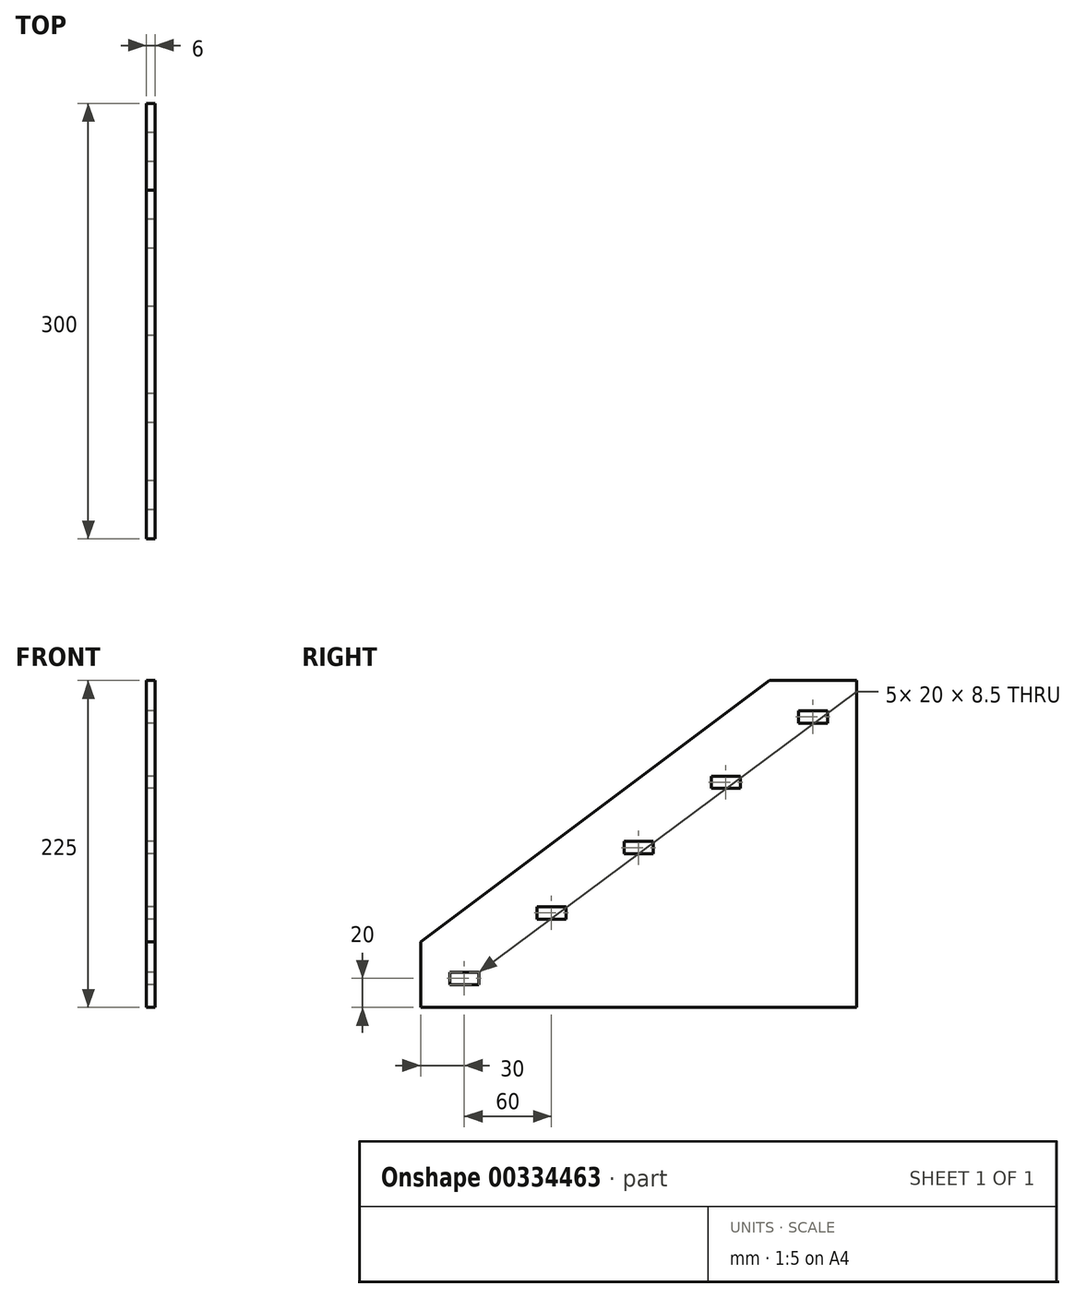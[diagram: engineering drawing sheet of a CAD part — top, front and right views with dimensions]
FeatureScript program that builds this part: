
annotation { "Feature Type Name" : "Feature", "Feature Type Description" : "" }
export const myFeature = defineFeature(function(context is Context, id is Id, definition is map)
    precondition{}
    {
        {
            var Q0;
            Q0=qCreatedBy(makeId("Right.planeOp"),FACE);
            var sketch = newSketch(context, id + "F0", { "sketchPlane" : qUnion([Q0])});
            skLineSegment(sketch, "E0", {"start": v(0, 0) * mm, "end": v(60, 0) * mm, "construction": true});
            skLineSegment(sketch, "E1", {"start": v(60, 0) * mm, "end": v(60, 45) * mm, "construction": true});
            skLineSegment(sketch, "E2", {"start": v(60, 45) * mm, "end": v(120, 45) * mm, "construction": true});
            skLineSegment(sketch, "E3", {"start": v(120, 45) * mm, "end": v(120, 90) * mm, "construction": true});
            skLineSegment(sketch, "E4", {"start": v(120, 90) * mm, "end": v(180, 90) * mm, "construction": true});
            skLineSegment(sketch, "E5", {"start": v(180, 90) * mm, "end": v(180, 135) * mm, "construction": true});
            skLineSegment(sketch, "E6", {"start": v(180, 135) * mm, "end": v(240, 135) * mm, "construction": true});
            skLineSegment(sketch, "E7", {"start": v(240, 135) * mm, "end": v(240, 180) * mm, "construction": true});
            skLineSegment(sketch, "E8", {"start": v(240, 180) * mm, "end": v(300, 180) * mm, "construction": true});
            skLineSegment(sketch, "E9.bottom", {"start": v(40, 4.25) * mm, "end": v(20, 4.25) * mm});
            skLineSegment(sketch, "E9.top", {"start": v(40, -4.25) * mm, "end": v(20, -4.25) * mm});
            skLineSegment(sketch, "E9.left", {"start": v(40, 4.25) * mm, "end": v(40, -4.25) * mm});
            skLineSegment(sketch, "E9.right", {"start": v(20, 4.25) * mm, "end": v(20, -4.25) * mm});
            skPoint(sketch, "E9.middle", {"position": v(30, 0) * mm});
            skLineSegment(sketch, "E10.bottom", {"start": v(100, 49.25) * mm, "end": v(80, 49.25) * mm});
            skLineSegment(sketch, "E10.top", {"start": v(100, 40.75) * mm, "end": v(80, 40.75) * mm});
            skLineSegment(sketch, "E10.left", {"start": v(100, 49.25) * mm, "end": v(100, 40.75) * mm});
            skLineSegment(sketch, "E10.right", {"start": v(80, 49.25) * mm, "end": v(80, 40.75) * mm});
            skPoint(sketch, "E10.middle", {"position": v(90, 45) * mm});
            skLineSegment(sketch, "E11.bottom", {"start": v(160, 94.25) * mm, "end": v(140, 94.25) * mm});
            skLineSegment(sketch, "E11.top", {"start": v(160, 85.75) * mm, "end": v(140, 85.75) * mm});
            skLineSegment(sketch, "E11.left", {"start": v(160, 94.25) * mm, "end": v(160, 85.75) * mm});
            skLineSegment(sketch, "E11.right", {"start": v(140, 94.25) * mm, "end": v(140, 85.75) * mm});
            skPoint(sketch, "E11.middle", {"position": v(150, 90) * mm});
            skLineSegment(sketch, "E12.bottom", {"start": v(200, 139.25) * mm, "end": v(220, 139.25) * mm});
            skLineSegment(sketch, "E12.top", {"start": v(200, 130.75) * mm, "end": v(220, 130.75) * mm});
            skLineSegment(sketch, "E12.left", {"start": v(200, 139.25) * mm, "end": v(200, 130.75) * mm});
            skLineSegment(sketch, "E12.right", {"start": v(220, 139.25) * mm, "end": v(220, 130.75) * mm});
            skPoint(sketch, "E12.middle", {"position": v(210, 135) * mm});
            skLineSegment(sketch, "E13.bottom", {"start": v(260, 184.25) * mm, "end": v(280, 184.25) * mm});
            skLineSegment(sketch, "E13.top", {"start": v(260, 175.75) * mm, "end": v(280, 175.75) * mm});
            skLineSegment(sketch, "E13.left", {"start": v(260, 184.25) * mm, "end": v(260, 175.75) * mm});
            skLineSegment(sketch, "E13.right", {"start": v(280, 184.25) * mm, "end": v(280, 175.75) * mm});
            skPoint(sketch, "E13.middle", {"position": v(270, 180) * mm});
            skLineSegment(sketch, "E14", {"start": v(0, 0) * mm, "end": v(0, 25) * mm});
            skLineSegment(sketch, "E15", {"start": v(300, 180) * mm, "end": v(300, 205) * mm});
            skLineSegment(sketch, "E16", {"start": v(300, 205) * mm, "end": v(240, 205) * mm});
            skLineSegment(sketch, "E17", {"start": v(240, 205) * mm, "end": v(0, 25) * mm});
            skLineSegment(sketch, "E18", {"start": v(300, 180) * mm, "end": v(300, 0) * mm});
            skLineSegment(sketch, "E19", {"start": v(300, 0) * mm, "end": v(300, -20) * mm});
            skLineSegment(sketch, "E20", {"start": v(300, -20) * mm, "end": v(0, -20) * mm});
            skLineSegment(sketch, "E21", {"start": v(0, -20) * mm, "end": v(0, 0) * mm});
            skSolve(sketch);
        }
        {
            var Q0;
            Q0 = qSketchRegion(id + "F0", true);
            extrude(context, id + "F1", {"entities" : qUnion([Q0]), "depth" : 6 * mm});
        }
    });
